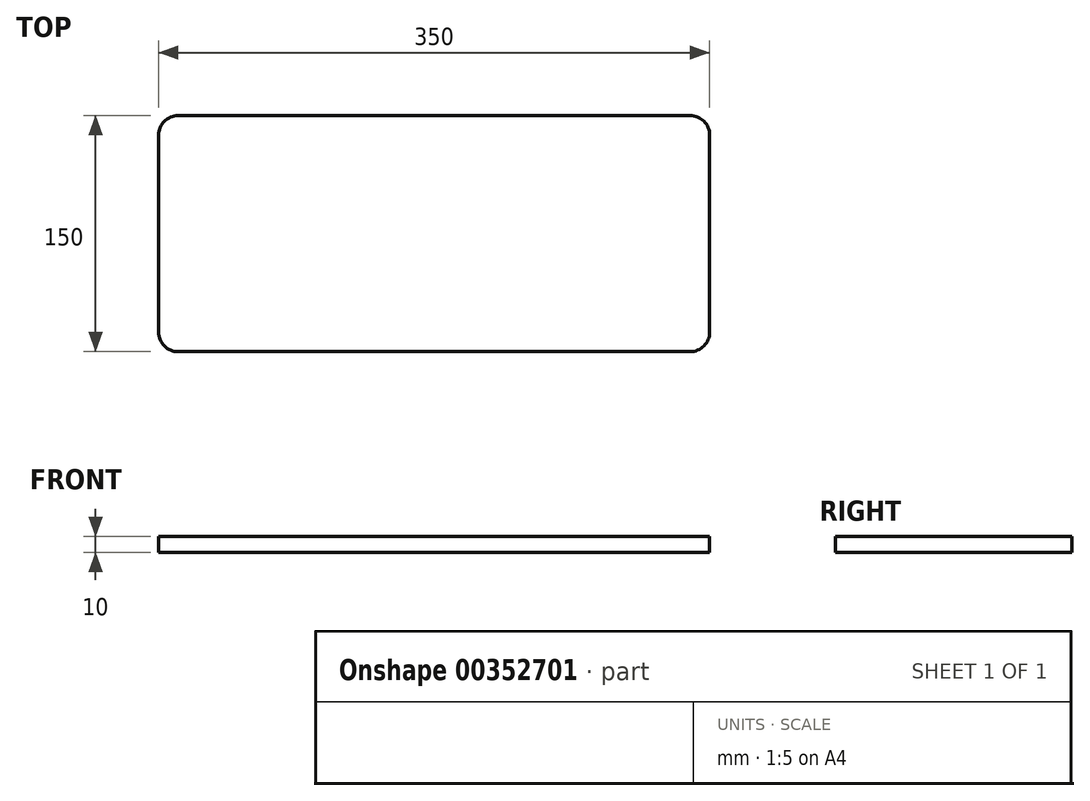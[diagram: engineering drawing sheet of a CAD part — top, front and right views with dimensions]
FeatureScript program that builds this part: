
annotation { "Feature Type Name" : "Feature", "Feature Type Description" : "" }
export const myFeature = defineFeature(function(context is Context, id is Id, definition is map)
    precondition{}
    {
        {
            var Q0;
            Q0=qCreatedBy(makeId("Top.planeOp"),FACE);
            var sketch = newSketch(context, id + "F0", { "sketchPlane" : qUnion([Q0])});
            skLineSegment(sketch, "E0.bottom", {"start": v(162.5, 75) * mm, "end": v(-162.5, 75) * mm});
            skLineSegment(sketch, "E0.top", {"start": v(162.5, -75) * mm, "end": v(-162.5, -75) * mm});
            skLineSegment(sketch, "E0.left", {"start": v(175, 62.5) * mm, "end": v(175, -62.5) * mm});
            skLineSegment(sketch, "E0.right", {"start": v(-175, 62.5) * mm, "end": v(-175, -62.5) * mm});
            skPoint(sketch, "E0.middle", {"position": v(0, 0) * mm});
            skPoint(sketch, "E1.visualSharp", {"position": v(-175, 75) * mm});
            skArc(sketch, "E1.filletArc", {"start": v(-162.5, 75) * mm, "mid": v(-171.34, 71.34) * mm, "end": v(-175, 62.5) * mm});
            skPoint(sketch, "E2.visualSharp", {"position": v(-175, -75) * mm});
            skArc(sketch, "E2.filletArc", {"start": v(-175, -62.5) * mm, "mid": v(-171.34, -71.34) * mm, "end": v(-162.5, -75) * mm});
            skPoint(sketch, "E3.visualSharp", {"position": v(175, -75) * mm});
            skArc(sketch, "E3.filletArc", {"start": v(162.5, -75) * mm, "mid": v(171.34, -71.34) * mm, "end": v(175, -62.5) * mm});
            skPoint(sketch, "E4.visualSharp", {"position": v(175, 75) * mm});
            skArc(sketch, "E4.filletArc", {"start": v(175, 62.5) * mm, "mid": v(171.34, 71.34) * mm, "end": v(162.5, 75) * mm});
            skSolve(sketch);
        }
        {
            var Q0;
            Q0 = qSketchRegion(id + "F0", true);
            extrude(context, id + "F1", {"entities" : qUnion([Q0]), "depth" : 10 * mm});
        }
    });
